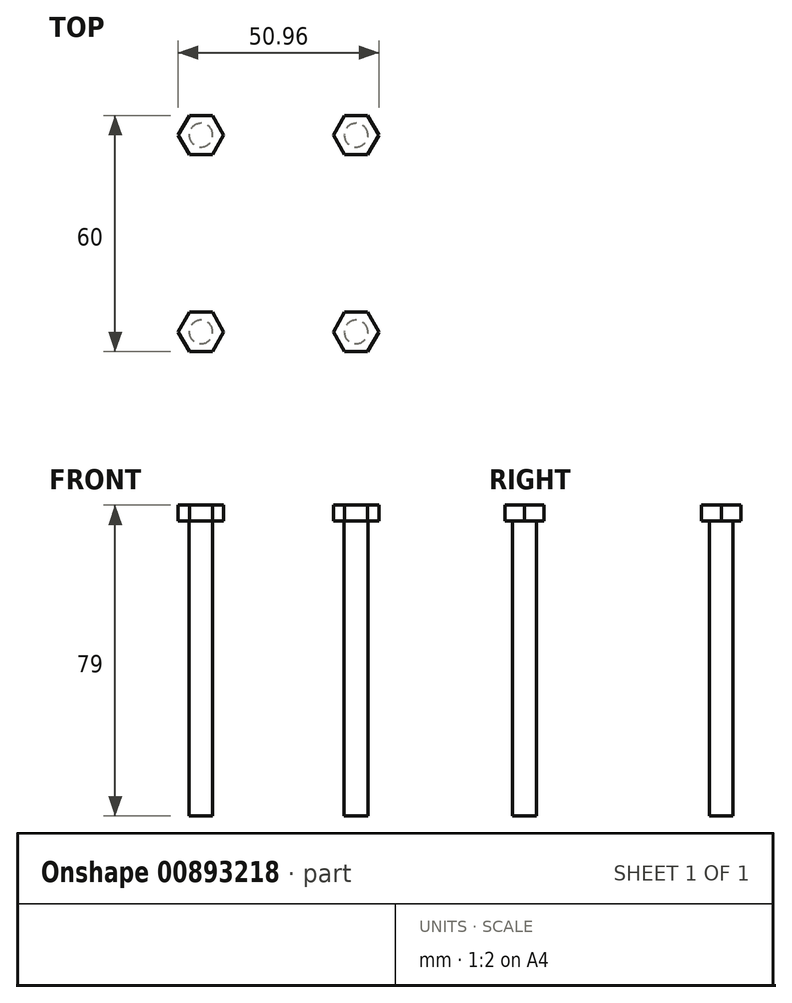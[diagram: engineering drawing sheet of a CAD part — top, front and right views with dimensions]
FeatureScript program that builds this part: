
annotation { "Feature Type Name" : "Feature", "Feature Type Description" : "" }
export const myFeature = defineFeature(function(context is Context, id is Id, definition is map)
    precondition{}
    {
        {
            var Q0;
            Q0=qCreatedBy(makeId("Top.planeOp"),FACE);
            var sketch = newSketch(context, id + "F0", { "sketchPlane" : qUnion([Q0])});
            skCircle(sketch, "E0", {"center": v(-8.52, 0) * mm, "radius": 3 * mm});
            skCircle(sketch, "E1", {"center": v(-19.7, 0) * mm, "radius": 3 * mm});
            skCircle(sketch, "E2", {"center": v(8.77, 0) * mm, "radius": 3 * mm});
            skCircle(sketch, "E3", {"center": v(16.9, 0) * mm, "radius": 3 * mm});
            skSolve(sketch);
        }
        {
            var Q0;
            Q0 = qSketchRegion(id + "F0", true);
            extrude(context, id + "F1", {"entities" : qUnion([Q0]), "depth" : 75 * mm, "offsetDistance" : 25 * mm});
        }
        {
            var Q0;
            Q0=makeQuery(id+"F1.opExtrude","CAP_FACE",FACE,{"disambiguationData":[OSD([sQuery(id+"F0.wireOp",EDGE,"E1")])],"isStart":false});
            var sketch = newSketch(context, id + "F2", { "sketchPlane" : qUnion([Q0])});
            skCircle(sketch, "E4.cCircle", {"center": v(-19.7, 0) * mm, "radius": 5 * mm, "construction": true});
            skLineSegment(sketch, "E4.0", {"start": v(-22.59, 5) * mm, "end": v(-16.82, 5) * mm});
            skLineSegment(sketch, "E4.1", {"start": v(-16.82, 5) * mm, "end": v(-13.93, 0) * mm});
            skLineSegment(sketch, "E4.2", {"start": v(-13.93, 0) * mm, "end": v(-16.82, -5) * mm});
            skLineSegment(sketch, "E4.3", {"start": v(-16.82, -5) * mm, "end": v(-22.59, -5) * mm});
            skLineSegment(sketch, "E4.4", {"start": v(-22.59, -5) * mm, "end": v(-25.48, 0) * mm});
            skLineSegment(sketch, "E4.5", {"start": v(-25.48, 0) * mm, "end": v(-22.59, 5) * mm});
            skPoint(sketch, "E4.0.midPoint", {"position": v(-19.7, 5) * mm});
            skSolve(sketch);
        }
        {
            var Q0;
            Q0 = qSketchRegion(id + "F2", true);
            extrude(context, id + "F3", {"entities" : qUnion([Q0]), "operationType" : NewBodyOperationType.ADD, "depth" : 4 * mm, "offsetDistance" : 25 * mm});
        }
        {
            var Q0;
            Q0=makeQuery(id+"F1.opExtrude","SWEPT_BODY",BODY,{"disambiguationData":[OSD([sQuery(id+"F0.wireOp",EDGE,"E3")])]});
            var Q1;
            Q1=makeQuery(id+"F1.opExtrude","SWEPT_BODY",BODY,{"disambiguationData":[OSD([sQuery(id+"F0.wireOp",EDGE,"E2")])]});
            deleteBodies(context, id + "F4", {"entities" : qUnion([Q0, Q1])});
        }
        {
            var Q0;
            Q0=makeQuery(id+"F1.opExtrude","SWEPT_BODY",BODY,{"disambiguationData":[OSD([sQuery(id+"F0.wireOp",EDGE,"E0")])]});
            deleteBodies(context, id + "F5", {"entities" : qUnion([Q0])});
        }
        {
            var Q0;
            Q0=makeQuery(id+"F1.opExtrude","SWEPT_BODY",BODY,{"disambiguationData":[OSD([sQuery(id+"F0.wireOp",EDGE,"E1")])]});
            var Q1;
            Q1=qCreatedBy(makeId("Right.planeOp"),FACE);
            mirror(context, id + "F6", {"entities" : qUnion([Q0]), "mirrorPlane" : qUnion([Q1])});
        }
        {
            var Q0;
            Q0=qCreatedBy(makeId("Front.planeOp"),FACE);
            cPlane(context, id + "F7", {"entities" : qUnion([Q0]), "cplaneType" : CPlaneType.OFFSET, "offset" : 25 * mm, "width" : 150 * mm, "height" : 150 * mm});
        }
        {
            var Q0;
            Q0=makeQuery(id+"F1.opExtrude","SWEPT_BODY",BODY,{"disambiguationData":[OSD([sQuery(id+"F0.wireOp",EDGE,"E1")])]});
            var Q1;
            Q1=qCreatedBy(id+"F7.planeOp",FACE);
            mirror(context, id + "F8", {"entities" : qUnion([Q0]), "mirrorPlane" : qUnion([Q1])});
        }
        {
            var Q0;
            Q0=makeQuery(id+"F6.opPattern","COPY",BODY,{"derivedFrom":makeQuery(id+"F1.opExtrude","SWEPT_BODY",BODY,{"disambiguationData":[OSD([sQuery(id+"F0.wireOp",EDGE,"E1")])]}),"instanceName":"1"});
            var Q1;
            Q1=qCreatedBy(id+"F7.planeOp",FACE);
            mirror(context, id + "F9", {"entities" : qUnion([Q0]), "mirrorPlane" : qUnion([Q1])});
        }
    });
